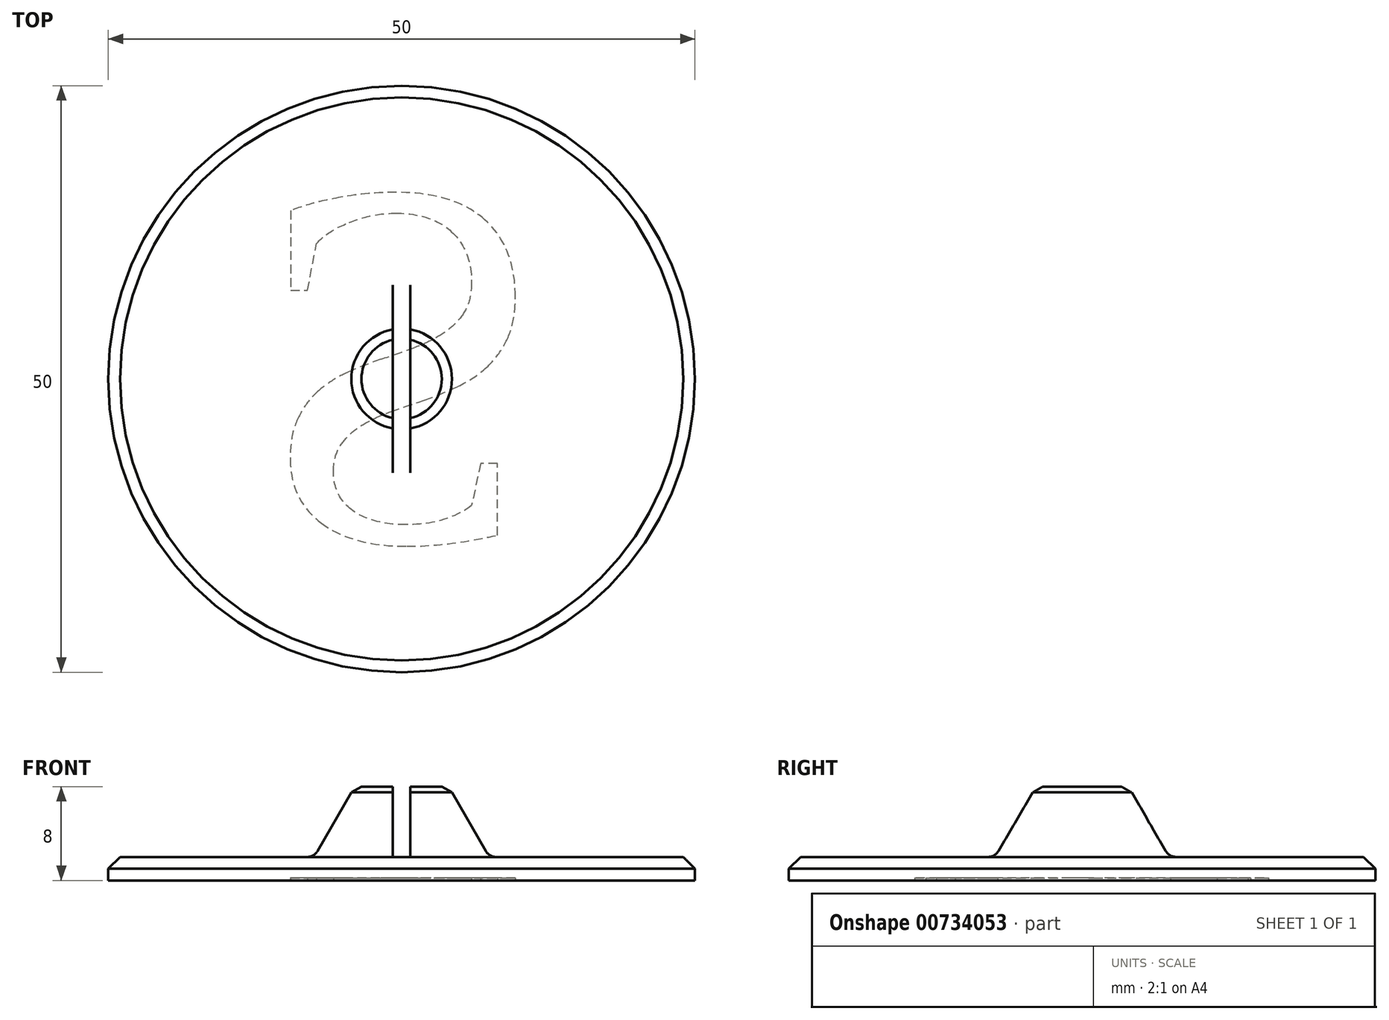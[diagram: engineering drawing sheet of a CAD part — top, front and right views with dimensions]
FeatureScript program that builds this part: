
annotation { "Feature Type Name" : "Feature", "Feature Type Description" : "" }
export const myFeature = defineFeature(function(context is Context, id is Id, definition is map)
    precondition{}
    {
        {
            var Q0;
            Q0=qCreatedBy(makeId("Front.planeOp"),FACE);
            var sketch = newSketch(context, id + "F0", { "sketchPlane" : qUnion([Q0])});
            skLineSegment(sketch, "E0", {"start": v(0, 0) * mm, "end": v(0, 8) * mm});
            skLineSegment(sketch, "E1", {"start": v(0, 0) * mm, "end": v(25, 0) * mm});
            skLineSegment(sketch, "E2", {"start": v(25, 0) * mm, "end": v(25, 2) * mm});
            skLineSegment(sketch, "E3", {"start": v(0, 8) * mm, "end": v(7.7, 8) * mm, "construction": true});
            skLineSegment(sketch, "E4", {"start": v(4, 8) * mm, "end": v(7.46, 2) * mm});
            skLineSegment(sketch, "E5", {"start": v(25, 2) * mm, "end": v(7.46, 2) * mm});
            skLineSegment(sketch, "E6", {"start": v(4, 8) * mm, "end": v(0, 8) * mm});
            skSolve(sketch);
        }
        {
            var Q0;
            Q0 = qSketchRegion(id + "F0", true);
            var Q1;
            Q1=sQuery(id+"F0.wireOp",EDGE,"E0");
            revolve(context, id + "F1", {"surfaceOperationType" : NewSurfaceOperationType.NEW, "entities" : qUnion([Q0]), "axis" : qUnion([Q1]), "revolveType" : RevolveType.FULL});
        }
        {
            var Q0;
            Q0=qCreatedBy(makeId("Front.planeOp"),FACE);
            var sketch = newSketch(context, id + "F2", { "sketchPlane" : qUnion([Q0])});
            skLineSegment(sketch, "E7.0", {"start": v(-15, 2) * mm, "end": v(15, 2) * mm, "construction": true});
            skPoint(sketch, "E8.middle", {"position": v(0, 2) * mm});
            skLineSegment(sketch, "E9.bottom", {"start": v(0.75, 2) * mm, "end": v(-0.75, 2) * mm});
            skLineSegment(sketch, "E9.top", {"start": v(0.75, 22) * mm, "end": v(-0.75, 22) * mm});
            skLineSegment(sketch, "E9.left", {"start": v(0.75, 2) * mm, "end": v(0.75, 22) * mm});
            skLineSegment(sketch, "E9.right", {"start": v(-0.75, 2) * mm, "end": v(-0.75, 22) * mm});
            skPoint(sketch, "E9.middle", {"position": v(0, 12) * mm});
            skSolve(sketch);
        }
        {
            var Q0;
            Q0 = qSketchRegion(id + "F2", true);
            extrude(context, id + "F3", {"entities" : qUnion([Q0]), "operationType" : NewBodyOperationType.REMOVE, "endBound" : BoundingType.THROUGH_ALL, "oppositeDirection" : true, "depth" : 25 * mm, "offsetDistance" : 25 * mm, "hasSecondDirection" : true, "secondDirectionBound" : SecondDirectionBoundingType.THROUGH_ALL, "secondDirectionOppositeDirection" : false, "secondDirectionDepth" : 25 * mm});
        }
        {
            var Q0;
            Q0=makeQuery(id+"F1.opRevolve","SWEPT_FACE",FACE,{"disambiguationData":[OSD([sQuery(id+"F0.wireOp",EDGE,"E1")])]});
            var sketch = newSketch(context, id + "F4", { "sketchPlane" : qUnion([Q0])});
            skText(sketch, "E10", { "text": "S", "fontName": "Tinos-Regular.ttf"});
            const initialGuessF4  = {"E10": [-0.0125, -0.01547, 1, 0, 0.03233]};
            skSetInitialGuess(sketch, initialGuessF4);
            skSolve(sketch);
        }
        {
            var Q0;
            Q0 = qSketchRegion(id + "F4", true);
            extrude(context, id + "F5", {"entities" : qUnion([Q0]), "operationType" : NewBodyOperationType.REMOVE, "oppositeDirection" : true, "depth" : 0.2 * mm, "offsetDistance" : 25 * mm});
        }
        {
            var Q0;
            Q0=makeQuery(id+"F1.opRevolve","SWEPT_EDGE",EDGE,{"disambiguationData":[OSD([sQuery(id+"F0.wireOp",EDGE,"E2"),sQuery(id+"F0.wireOp",EDGE,"E5")])]});
            var Q1;
            {var subQ0=sQuery(id+"F0.wireOp",EDGE,"E4");var subQ1=sQuery(id+"F0.wireOp",EDGE,"E6");Q1=makeQuery(id+"F3.boolean.opBoolean","SPLIT",EDGE,{"disambiguationData":[TD([makeQuery(id+"F3.opExtrude","SWEPT_FACE",FACE,{"disambiguationData":[OSD([sQuery(id+"F2.wireOp",EDGE,"E9.left")])]})])],"derivedFrom":makeQuery(id+"F1.opRevolve","SWEPT_EDGE",EDGE,{"disambiguationData":[OSD([subQ0,subQ1])]})});}
            var Q2;
            {var subQ0=sQuery(id+"F0.wireOp",EDGE,"E4");var subQ1=sQuery(id+"F0.wireOp",EDGE,"E6");Q2=makeQuery(id+"F3.boolean.opBoolean","SPLIT",EDGE,{"disambiguationData":[TD([makeQuery(id+"F3.opExtrude","SWEPT_FACE",FACE,{"disambiguationData":[OSD([sQuery(id+"F2.wireOp",EDGE,"E9.right")])]})])],"derivedFrom":makeQuery(id+"F1.opRevolve","SWEPT_EDGE",EDGE,{"disambiguationData":[OSD([subQ0,subQ1])]})});}
            chamfer(context, id + "F6", {"entities" : qUnion([Q0, Q1, Q2]), "width" : 1 * mm, "tangentPropagation" : true});
        }
        {
            var Q0;
            {var subQ0=sQuery(id+"F0.wireOp",EDGE,"E4");var subQ1=sQuery(id+"F0.wireOp",EDGE,"E5");Q0=makeQuery(id+"F3.boolean.opBoolean","SPLIT",EDGE,{"disambiguationData":[TD([makeQuery(id+"F3.opExtrude","SWEPT_FACE",FACE,{"disambiguationData":[OSD([sQuery(id+"F2.wireOp",EDGE,"E9.right")])]})])],"derivedFrom":makeQuery(id+"F1.opRevolve","SWEPT_EDGE",EDGE,{"disambiguationData":[OSD([subQ0,subQ1])]})});}
            var Q1;
            {var subQ0=sQuery(id+"F0.wireOp",EDGE,"E4");var subQ1=sQuery(id+"F0.wireOp",EDGE,"E5");Q1=makeQuery(id+"F3.boolean.opBoolean","SPLIT",EDGE,{"disambiguationData":[TD([makeQuery(id+"F3.opExtrude","SWEPT_FACE",FACE,{"disambiguationData":[OSD([sQuery(id+"F2.wireOp",EDGE,"E9.left")])]})])],"derivedFrom":makeQuery(id+"F1.opRevolve","SWEPT_EDGE",EDGE,{"disambiguationData":[OSD([subQ0,subQ1])]})});}
            fillet(context, id + "F7", {"entities" : qUnion([Q0, Q1]), "radius" : 1 * mm, "tangentPropagation" : true, "allowEdgeOverflow" : false});
        }
    });
